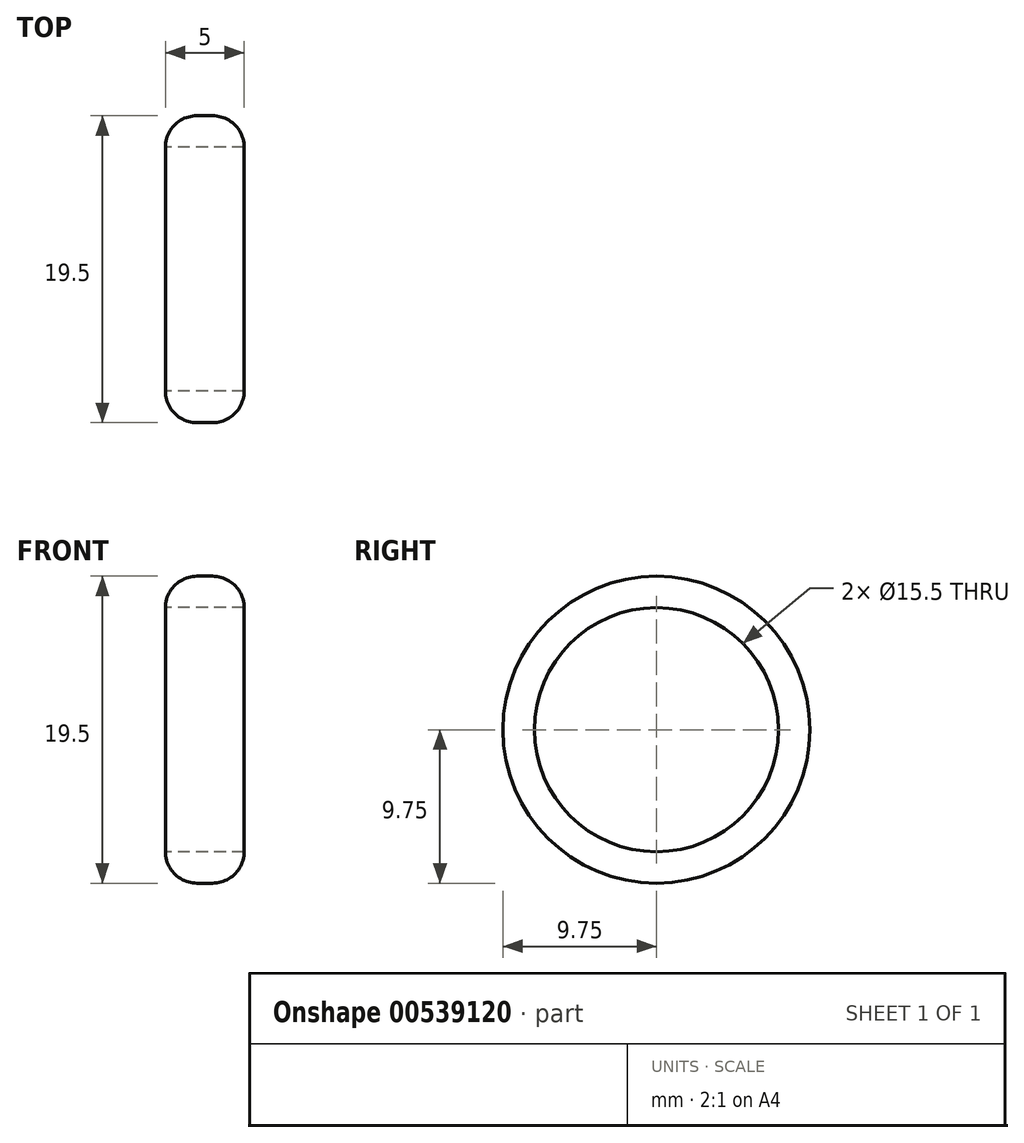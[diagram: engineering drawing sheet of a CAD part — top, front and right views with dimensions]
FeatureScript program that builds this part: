
annotation { "Feature Type Name" : "Feature", "Feature Type Description" : "" }
export const myFeature = defineFeature(function(context is Context, id is Id, definition is map)
    precondition{}
    {
        {
            var Q0;
            Q0=qCreatedBy(makeId("Right.planeOp"),FACE);
            var sketch = newSketch(context, id + "F0", { "sketchPlane" : qUnion([Q0])});
            skCircle(sketch, "E0", {"center": v(0, 0) * mm, "radius": 7.75 * mm});
            skCircle(sketch, "E1", {"center": v(0, 0) * mm, "radius": 9.75 * mm});
            skSolve(sketch);
        }
        {
            var Q0;
            Q0 = qSketchRegion(id + "F0", true);
            extrude(context, id + "F1", {"entities" : qUnion([Q0]), "depth" : 5 * mm, "offsetDistance" : 25.4 * mm});
        }
        {
            var Q0;
            Q0=makeQuery(id+"F1.opExtrude","CAP_EDGE",EDGE,{"disambiguationData":[OSD([sQuery(id+"F0.wireOp",EDGE,"E1")])],"isStart":true});
            fillet(context, id + "F2", {"entities" : qUnion([Q0]), "radius" : 2 * mm, "tangentPropagation" : true, "allowEdgeOverflow" : false});
        }
        {
            var Q0;
            Q0=makeQuery(id+"F1.opExtrude","CAP_EDGE",EDGE,{"disambiguationData":[OSD([sQuery(id+"F0.wireOp",EDGE,"E1")])],"isStart":false});
            fillet(context, id + "F3", {"entities" : qUnion([Q0]), "radius" : 2 * mm, "tangentPropagation" : true, "allowEdgeOverflow" : false});
        }
    });
